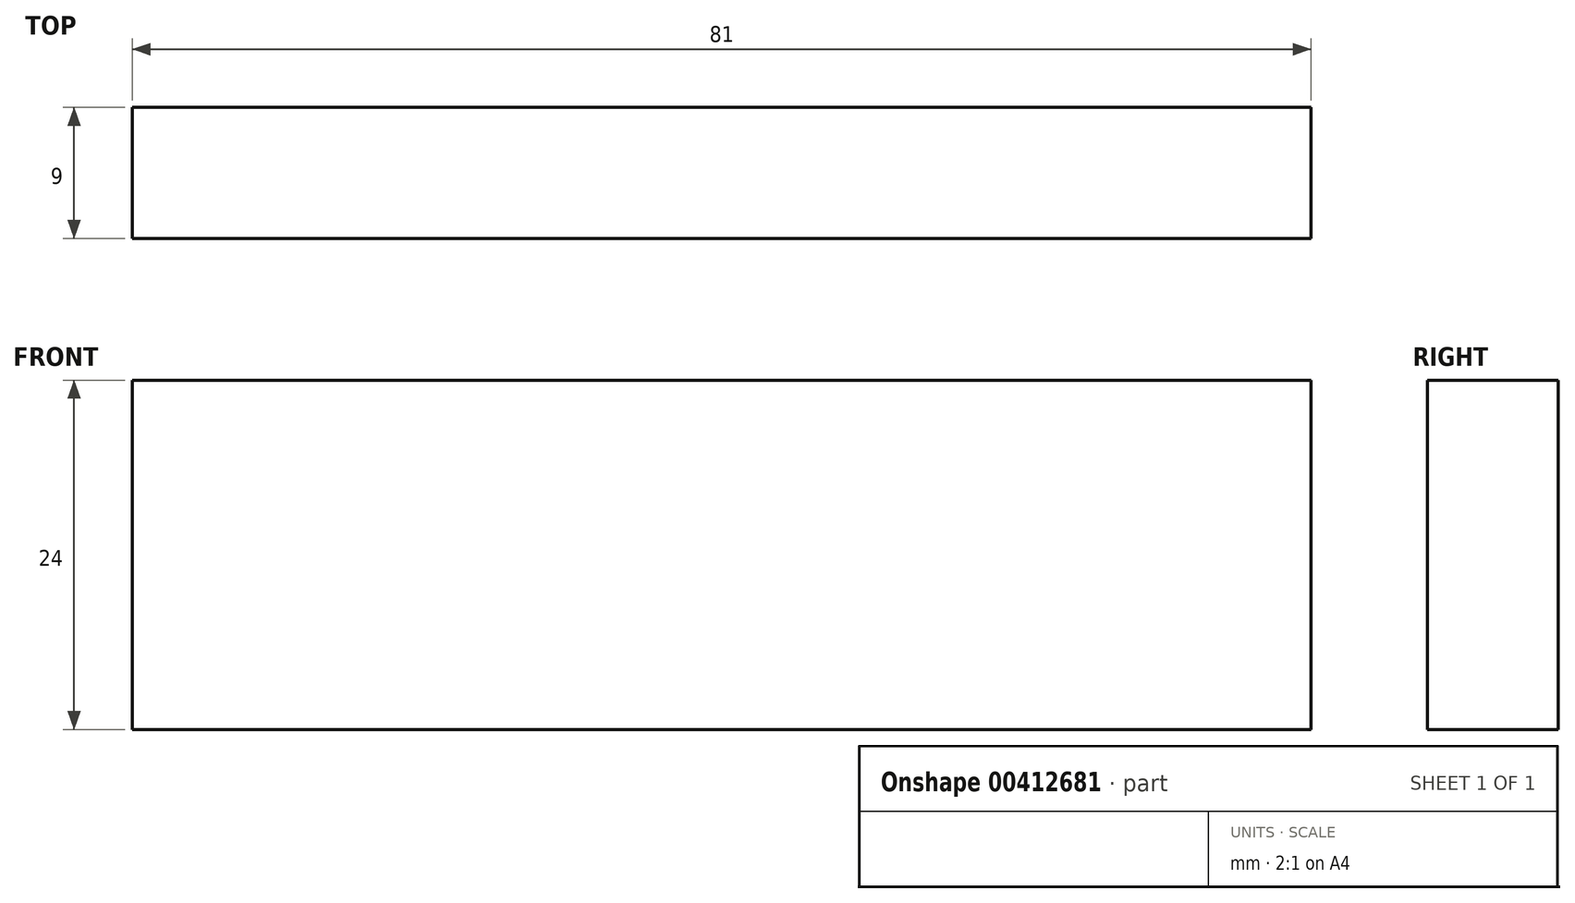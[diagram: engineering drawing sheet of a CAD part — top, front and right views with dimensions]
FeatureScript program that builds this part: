
annotation { "Feature Type Name" : "Feature", "Feature Type Description" : "" }
export const myFeature = defineFeature(function(context is Context, id is Id, definition is map)
    precondition{}
    {
        {
            var Q0;
            Q0=qCreatedBy(makeId("Front.planeOp"),FACE);
            var sketch = newSketch(context, id + "F0", { "sketchPlane" : qUnion([Q0])});
            skLineSegment(sketch, "E0.bottom", {"start": v(40.5, 12) * mm, "end": v(-40.5, 12) * mm});
            skLineSegment(sketch, "E0.top", {"start": v(40.5, -12) * mm, "end": v(-40.5, -12) * mm});
            skLineSegment(sketch, "E0.left", {"start": v(40.5, 12) * mm, "end": v(40.5, -12) * mm});
            skLineSegment(sketch, "E0.right", {"start": v(-40.5, 12) * mm, "end": v(-40.5, -12) * mm});
            skPoint(sketch, "E0.middle", {"position": v(0, 0) * mm});
            skSolve(sketch);
        }
        {
            var Q0;
            Q0=makeQuery(id+"F0.imprint","IMPRINT",FACE,{"disambiguationData":[TD([[makeQuery(id+"F0.imprint","IMPRINT",EDGE,{"derivedFrom":sQuery(id+"F0.wireOp",EDGE,"E0.bottom")}),1.0]])]});
            extrude(context, id + "F1", {"entities" : qUnion([Q0]), "depth" : 9 * mm, "offsetDistance" : 25 * mm});
        }
    });
